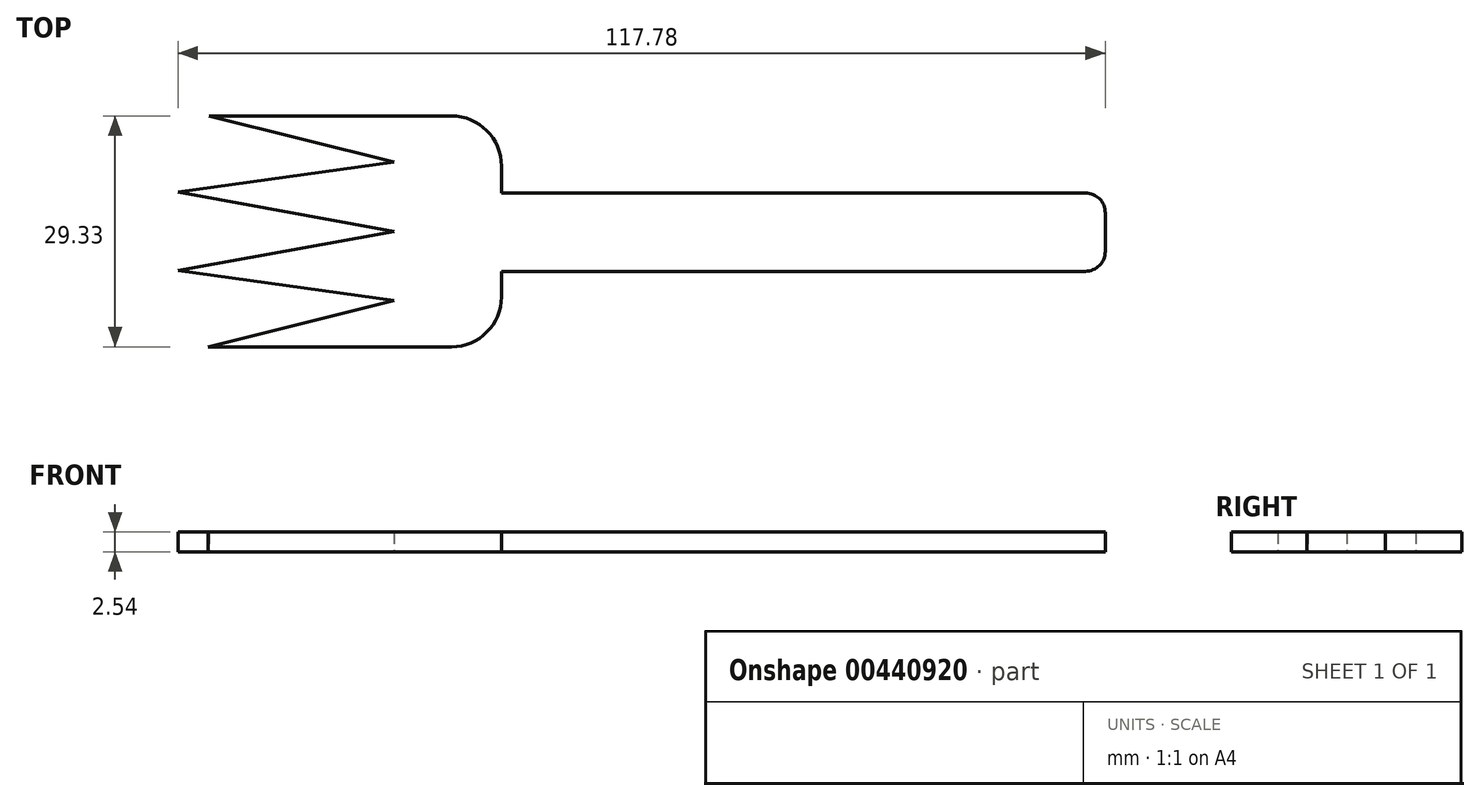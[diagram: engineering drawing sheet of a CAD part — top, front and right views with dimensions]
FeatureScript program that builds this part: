
annotation { "Feature Type Name" : "Feature", "Feature Type Description" : "" }
export const myFeature = defineFeature(function(context is Context, id is Id, definition is map)
    precondition{}
    {
        {
            var Q0;
            Q0=qCreatedBy(makeId("Top.planeOp"),FACE);
            var sketch = newSketch(context, id + "F0", { "sketchPlane" : qUnion([Q0])});
            skLineSegment(sketch, "E0.bottom", {"start": v(-18.83, 4.88) * mm, "end": v(55.33, 4.88) * mm});
            skLineSegment(sketch, "E0.top", {"start": v(-18.83, -5.08) * mm, "end": v(55.33, -5.08) * mm});
            skLineSegment(sketch, "E0.right", {"start": v(57.87, 2.34) * mm, "end": v(57.87, -2.54) * mm});
            skLineSegment(sketch, "E1.bottom", {"start": v(-56.08, 14.65) * mm, "end": v(-25.18, 14.65) * mm});
            skLineSegment(sketch, "E1.top", {"start": v(-56.08, -14.68) * mm, "end": v(-25.18, -14.68) * mm});
            skLineSegment(sketch, "E1.right", {"start": v(-18.83, 8.3) * mm, "end": v(-18.83, 4.88) * mm});
            skLineSegment(sketch, "E2", {"start": v(-56.08, -14.68) * mm, "end": v(-32.47, -8.78) * mm});
            skLineSegment(sketch, "E3", {"start": v(-32.47, -8.78) * mm, "end": v(-59.91, -4.97) * mm});
            skLineSegment(sketch, "E4", {"start": v(-59.91, -4.97) * mm, "end": v(-32.47, 0) * mm});
            skLineSegment(sketch, "E5.MirrorCS", {"start": v(-59.91, 4.97) * mm, "end": v(-32.47, 0) * mm});
            skLineSegment(sketch, "E6.MirrorCS", {"start": v(-32.47, 8.78) * mm, "end": v(-59.91, 4.97) * mm});
            skLineSegment(sketch, "E7.MirrorCS", {"start": v(-56.08, 14.68) * mm, "end": v(-32.47, 8.78) * mm});
            skPoint(sketch, "E8.visualSharp", {"position": v(57.87, 4.88) * mm});
            skArc(sketch, "E8.filletArc", {"start": v(57.87, 2.34) * mm, "mid": v(57.12, 4.14) * mm, "end": v(55.33, 4.88) * mm});
            skPoint(sketch, "E9.visualSharp", {"position": v(57.87, -5.08) * mm});
            skArc(sketch, "E9.filletArc", {"start": v(55.33, -5.08) * mm, "mid": v(57.12, -4.34) * mm, "end": v(57.87, -2.54) * mm});
            skPoint(sketch, "E10.visualSharp", {"position": v(-18.83, 14.65) * mm});
            skArc(sketch, "E10.filletArc", {"start": v(-18.83, 8.3) * mm, "mid": v(-20.7, 12.79) * mm, "end": v(-25.18, 14.65) * mm});
            skPoint(sketch, "E11.visualSharp", {"position": v(-18.83, -14.68) * mm});
            skArc(sketch, "E11.filletArc", {"start": v(-25.18, -14.68) * mm, "mid": v(-20.7, -12.82) * mm, "end": v(-18.83, -8.33) * mm});
            skLineSegment(sketch, "E12.trimOffspring", {"start": v(-18.83, -5.08) * mm, "end": v(-18.83, -8.33) * mm});
            skSolve(sketch);
        }
        {
            var Q0;
            Q0 = qSketchRegion(id + "F0", true);
            extrude(context, id + "F1", {"entities" : qUnion([Q0]), "depth" : 2.54 * mm});
        }
    });
